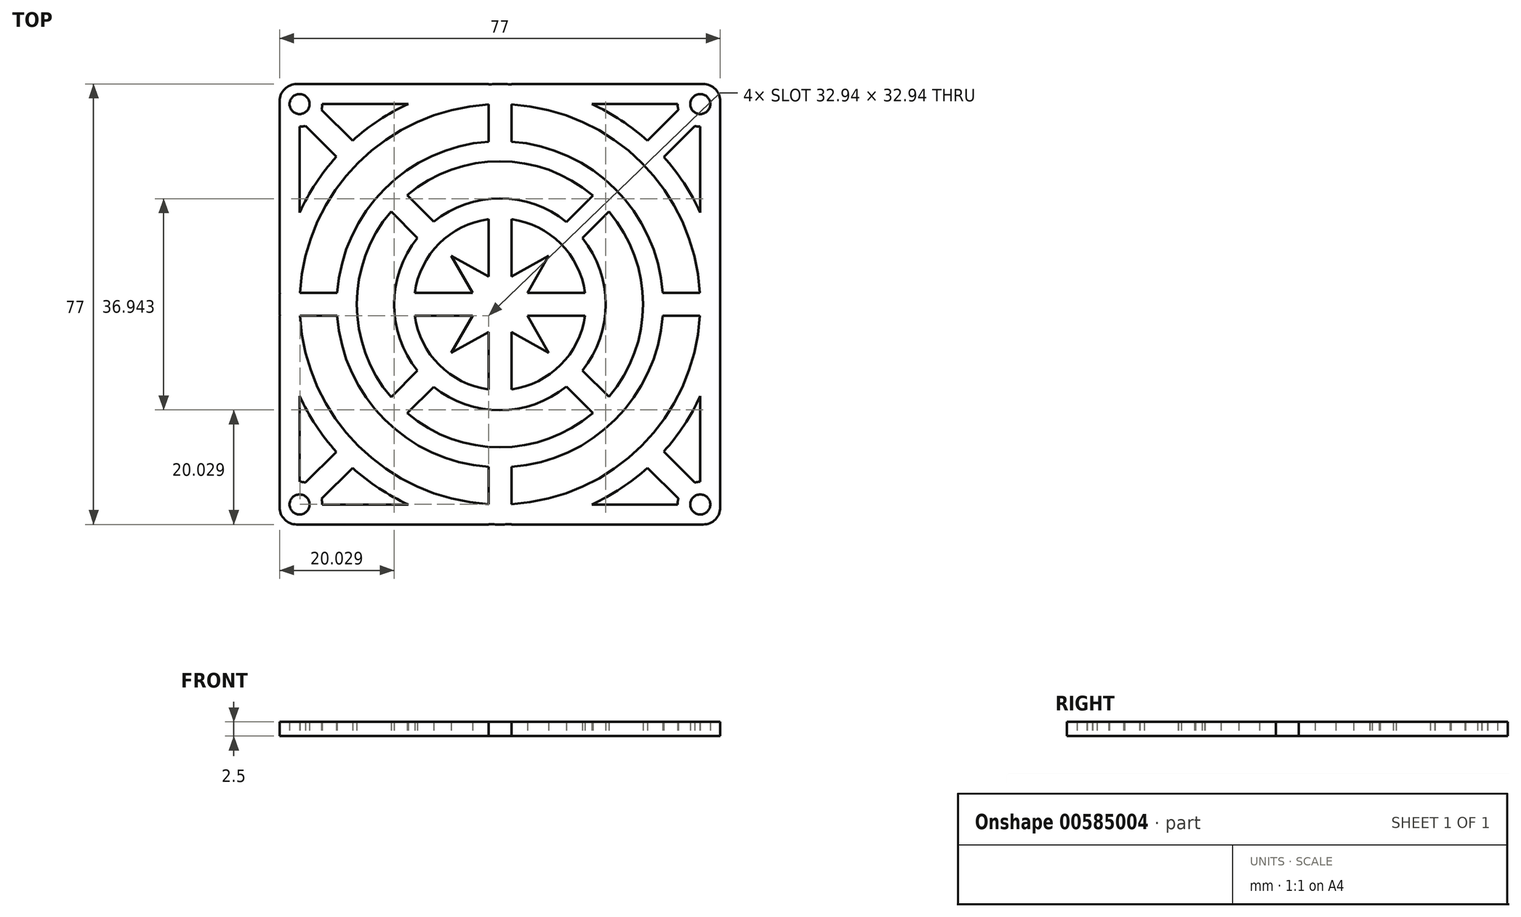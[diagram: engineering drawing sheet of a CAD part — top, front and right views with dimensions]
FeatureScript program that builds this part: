
annotation { "Feature Type Name" : "Feature", "Feature Type Description" : "" }
export const myFeature = defineFeature(function(context is Context, id is Id, definition is map)
    precondition{}
    {
        {
            var Q0;
            Q0=qCreatedBy(makeId("Top.planeOp"),FACE);
            var sketch = newSketch(context, id + "F0", { "sketchPlane" : qUnion([Q0])});
            skLineSegment(sketch, "E0.bottom", {"start": v(-31.05, -35) * mm, "end": v(-16.04, -35) * mm});
            skLineSegment(sketch, "E0.top", {"start": v(-31.05, 35) * mm, "end": v(-16.04, 35) * mm});
            skPoint(sketch, "E0.middle", {"position": v(0, 0) * mm});
            skPoint(sketch, "E1.MirrorCS.end.orphan", {"position": v(34.64, -4.98) * mm});
            skPoint(sketch, "E1.MirrorCS.start.orphan", {"position": v(-34.64, -4.98) * mm});
            skPoint(sketch, "E2.orphan", {"position": v(-34.64, 8.3) * mm});
            skPoint(sketch, "E3.orphan", {"position": v(-34.64, -8.3) * mm});
            skPoint(sketch, "E4.orphan", {"position": v(-34.64, -11.63) * mm});
            skPoint(sketch, "E5.orphan", {"position": v(34.64, -11.63) * mm});
            skPoint(sketch, "E6.orphan", {"position": v(34.64, -8.3) * mm});
            skPoint(sketch, "E7.right.end.orphan", {"position": v(34.64, 8.3) * mm});
            skPoint(sketch, "E8.orphan", {"position": v(-34.64, 4.98) * mm});
            skPoint(sketch, "E9.orphan", {"position": v(34.64, 4.98) * mm});
            skCircle(sketch, "E10", {"center": v(-35, 35) * mm, "radius": 1.75 * mm});
            skCircle(sketch, "E11.MirrorC", {"center": v(35, 35) * mm, "radius": 1.75 * mm});
            skCircle(sketch, "E12.MirrorC", {"center": v(35, -35) * mm, "radius": 1.75 * mm});
            skCircle(sketch, "E13.MirrorC", {"center": v(-35, -35) * mm, "radius": 1.75 * mm});
            skLineSegment(sketch, "E14.bottom", {"start": v(-35.5, -38.5) * mm, "end": v(35.5, -38.5) * mm});
            skLineSegment(sketch, "E14.top", {"start": v(-35.5, 38.5) * mm, "end": v(35.5, 38.5) * mm});
            skLineSegment(sketch, "E14.left", {"start": v(-38.5, -35.5) * mm, "end": v(-38.5, 35.5) * mm});
            skLineSegment(sketch, "E14.right", {"start": v(38.5, -35.5) * mm, "end": v(38.5, 35.5) * mm});
            skPoint(sketch, "E15.visualSharp", {"position": v(38.5, 38.5) * mm});
            skArc(sketch, "E15.filletArc", {"start": v(38.5, 35.5) * mm, "mid": v(37.62, 37.62) * mm, "end": v(35.5, 38.5) * mm});
            skPoint(sketch, "E16.visualSharp", {"position": v(38.5, -38.5) * mm});
            skArc(sketch, "E16.filletArc", {"start": v(35.5, -38.5) * mm, "mid": v(37.62, -37.62) * mm, "end": v(38.5, -35.5) * mm});
            skPoint(sketch, "E17.visualSharp", {"position": v(-38.5, -38.5) * mm});
            skArc(sketch, "E17.filletArc", {"start": v(-38.5, -35.5) * mm, "mid": v(-37.62, -37.62) * mm, "end": v(-35.5, -38.5) * mm});
            skPoint(sketch, "E18.visualSharp", {"position": v(-38.5, 38.5) * mm});
            skArc(sketch, "E18.filletArc", {"start": v(-35.5, 38.5) * mm, "mid": v(-37.62, 37.62) * mm, "end": v(-38.5, 35.5) * mm});
            skArc(sketch, "E19", {"start": v(-28.58, 25.8) * mm, "mid": v(-32.16, 21.16) * mm, "end": v(-35, 16.04) * mm});
            skArc(sketch, "E20", {"start": v(-2, 34.94) * mm, "mid": v(-24.75, 24.75) * mm, "end": v(-34.94, 2) * mm});
            skArc(sketch, "E21", {"start": v(-2, 28.43) * mm, "mid": v(-20.15, 20.15) * mm, "end": v(-28.43, 2) * mm});
            skArc(sketch, "E22", {"start": v(-19.02, 16.23) * mm, "mid": v(-25, 0) * mm, "end": v(-19.02, -16.23) * mm});
            skArc(sketch, "E23", {"start": v(-14.4, 11.6) * mm, "mid": v(-18.5, 0) * mm, "end": v(-14.4, -11.6) * mm});
            skArc(sketch, "E24", {"start": v(-2, 14.87) * mm, "mid": v(-10.6, 10.6) * mm, "end": v(-14.87, 2) * mm});
            skLineSegment(sketch, "E25.bottom", {"start": v(-2, -38.5) * mm, "end": v(2, -38.5) * mm});
            skLineSegment(sketch, "E25.top", {"start": v(-2, 38.5) * mm, "end": v(2, 38.5) * mm});
            skLineSegment(sketch, "E25.left", {"start": v(-2, -38.5) * mm, "end": v(-2, -38.45) * mm});
            skLineSegment(sketch, "E25.right", {"start": v(2, -38.5) * mm, "end": v(2, -38.45) * mm});
            skLineSegment(sketch, "E26.bottom", {"start": v(-38.5, -2) * mm, "end": v(-38.45, -2) * mm});
            skLineSegment(sketch, "E26.top", {"start": v(-38.5, 2) * mm, "end": v(-38.45, 2) * mm});
            skLineSegment(sketch, "E26.left", {"start": v(-38.5, -2) * mm, "end": v(-38.5, 2) * mm});
            skLineSegment(sketch, "E26.right", {"start": v(38.5, -2) * mm, "end": v(38.5, 2) * mm});
            skArc(sketch, "E27", {"start": v(-35, 31.05) * mm, "mid": v(-34.48, 31.08) * mm, "end": v(-33.97, 31.18) * mm});
            skArc(sketch, "E28.MirrorCS", {"start": v(35, 31.05) * mm, "mid": v(34.51, 31.08) * mm, "end": v(34.03, 31.17) * mm});
            skArc(sketch, "E29.MirrorCS", {"start": v(35, -31.05) * mm, "mid": v(34.51, -31.08) * mm, "end": v(34.03, -31.17) * mm});
            skArc(sketch, "E30.MirrorCS", {"start": v(-35, -31.05) * mm, "mid": v(-34.48, -31.08) * mm, "end": v(-33.97, -31.18) * mm});
            skLineSegment(sketch, "E31.trimOffspring", {"start": v(35, -31.05) * mm, "end": v(35, -16.04) * mm});
            skArc(sketch, "E32.trimOffspring", {"start": v(31.18, -33.97) * mm, "mid": v(31.08, -34.48) * mm, "end": v(31.05, -35) * mm});
            skLineSegment(sketch, "E33.trimOffspring", {"start": v(-35, -31.05) * mm, "end": v(-35, -16.04) * mm});
            skLineSegment(sketch, "E34.trimOffspring", {"start": v(16.04, 35) * mm, "end": v(31.05, 35) * mm});
            skLineSegment(sketch, "E35.trimOffspring", {"start": v(-25.75, 28.62) * mm, "end": v(-31.17, 34.03) * mm});
            skLineSegment(sketch, "E36.trimOffspring", {"start": v(-28.58, 25.8) * mm, "end": v(-33.97, 31.18) * mm});
            skLineSegment(sketch, "E37.trimOffspring", {"start": v(-11.57, 14.43) * mm, "end": v(-16.19, 19.05) * mm});
            skLineSegment(sketch, "E38.trimOffspring", {"start": v(-14.4, 11.6) * mm, "end": v(-19.02, 16.23) * mm});
            skLineSegment(sketch, "E39.trimOffspring", {"start": v(-2, 28.43) * mm, "end": v(-2, 35) * mm});
            skLineSegment(sketch, "E40.trimOffspring", {"start": v(2, 28.43) * mm, "end": v(2, 35) * mm});
            skLineSegment(sketch, "E41.trimOffspring", {"start": v(-2, 38.45) * mm, "end": v(-2, 38.5) * mm});
            skLineSegment(sketch, "E42.trimOffspring", {"start": v(2, 38.45) * mm, "end": v(2, 38.5) * mm});
            skLineSegment(sketch, "E43.trimOffspring", {"start": v(25.8, 28.58) * mm, "end": v(31.18, 33.97) * mm});
            skLineSegment(sketch, "E44.trimOffspring", {"start": v(28.62, 25.75) * mm, "end": v(34.03, 31.17) * mm});
            skArc(sketch, "E45.trimOffspring", {"start": v(25.8, 28.58) * mm, "mid": v(21.16, 32.16) * mm, "end": v(16.04, 35) * mm});
            skArc(sketch, "E46.trimOffspring", {"start": v(16.23, 19.02) * mm, "mid": v(0.02, 25) * mm, "end": v(-16.19, 19.05) * mm});
            skArc(sketch, "E47.trimOffspring", {"start": v(11.6, 14.4) * mm, "mid": v(0.02, 18.5) * mm, "end": v(-11.57, 14.43) * mm});
            skLineSegment(sketch, "E48.trimOffspring", {"start": v(11.6, 14.4) * mm, "end": v(16.23, 19.02) * mm});
            skLineSegment(sketch, "E49.trimOffspring", {"start": v(14.43, 11.57) * mm, "end": v(19.05, 16.19) * mm});
            skLineSegment(sketch, "E50.trimOffspring", {"start": v(35, 16.04) * mm, "end": v(35, 31.05) * mm});
            skLineSegment(sketch, "E51.trimOffspring", {"start": v(38.45, 2) * mm, "end": v(38.5, 2) * mm});
            skLineSegment(sketch, "E52.trimOffspring", {"start": v(38.45, -2) * mm, "end": v(38.5, -2) * mm});
            skArc(sketch, "E53.trimOffspring", {"start": v(34.94, 2) * mm, "mid": v(24.75, 24.75) * mm, "end": v(2, 34.94) * mm});
            skLineSegment(sketch, "E54.trimOffspring", {"start": v(28.43, 2) * mm, "end": v(35, 2) * mm});
            skLineSegment(sketch, "E55.trimOffspring", {"start": v(28.43, -2) * mm, "end": v(35, -2) * mm});
            skArc(sketch, "E56.trimOffspring", {"start": v(28.43, 2) * mm, "mid": v(20.15, 20.15) * mm, "end": v(2, 28.43) * mm});
            skArc(sketch, "E57.trimOffspring", {"start": v(14.87, 2) * mm, "mid": v(10.6, 10.6) * mm, "end": v(2, 14.87) * mm});
            skLineSegment(sketch, "E58.trimOffspring", {"start": v(28.62, -25.75) * mm, "end": v(34.03, -31.17) * mm});
            skLineSegment(sketch, "E59.trimOffspring", {"start": v(25.8, -28.58) * mm, "end": v(31.18, -33.97) * mm});
            skArc(sketch, "E60.trimOffspring", {"start": v(28.62, -25.75) * mm, "mid": v(32.18, -21.14) * mm, "end": v(35, -16.04) * mm});
            skArc(sketch, "E61.trimOffspring", {"start": v(19.05, -16.19) * mm, "mid": v(25, 0) * mm, "end": v(19.05, 16.19) * mm});
            skLineSegment(sketch, "E62.trimOffspring", {"start": v(14.43, -11.57) * mm, "end": v(19.05, -16.19) * mm});
            skLineSegment(sketch, "E63.trimOffspring", {"start": v(11.6, -14.4) * mm, "end": v(16.23, -19.02) * mm});
            skArc(sketch, "E64.trimOffspring", {"start": v(14.43, -11.57) * mm, "mid": v(18.5, 0) * mm, "end": v(14.43, 11.57) * mm});
            skLineSegment(sketch, "E65.trimOffspring", {"start": v(16.04, -35) * mm, "end": v(31.05, -35) * mm});
            skLineSegment(sketch, "E66.trimOffspring", {"start": v(-2, -35) * mm, "end": v(-2, -28.43) * mm});
            skLineSegment(sketch, "E67.trimOffspring", {"start": v(2, -35) * mm, "end": v(2, -28.43) * mm});
            skArc(sketch, "E68.trimOffspring", {"start": v(2, -34.94) * mm, "mid": v(24.75, -24.75) * mm, "end": v(34.94, -2) * mm});
            skArc(sketch, "E69.trimOffspring", {"start": v(2, -28.43) * mm, "mid": v(20.15, -20.15) * mm, "end": v(28.43, -2) * mm});
            skLineSegment(sketch, "E70.trimOffspring", {"start": v(-2, -14.87) * mm, "end": v(-2, -4.86) * mm});
            skLineSegment(sketch, "E71.trimOffspring", {"start": v(2, -14.87) * mm, "end": v(2, -4.8) * mm});
            skArc(sketch, "E72.trimOffspring", {"start": v(2, -14.87) * mm, "mid": v(10.6, -10.6) * mm, "end": v(14.87, -2) * mm});
            skArc(sketch, "E73.trimOffspring", {"start": v(-31.17, -34.03) * mm, "mid": v(-31.08, -34.51) * mm, "end": v(-31.05, -35) * mm});
            skArc(sketch, "E74.trimOffspring", {"start": v(31.18, 33.97) * mm, "mid": v(31.08, 34.48) * mm, "end": v(31.05, 35) * mm});
            skArc(sketch, "E75.trimOffspring", {"start": v(-31.17, 34.03) * mm, "mid": v(-31.08, 34.51) * mm, "end": v(-31.05, 35) * mm});
            skArc(sketch, "E76.trimOffspring", {"start": v(-25.75, -28.62) * mm, "mid": v(-21.14, -32.18) * mm, "end": v(-16.04, -35) * mm});
            skLineSegment(sketch, "E77.trimOffspring", {"start": v(-28.58, -25.8) * mm, "end": v(-33.97, -31.18) * mm});
            skLineSegment(sketch, "E78.trimOffspring", {"start": v(-25.75, -28.62) * mm, "end": v(-31.17, -34.03) * mm});
            skArc(sketch, "E79.trimOffspring", {"start": v(-16.19, -19.05) * mm, "mid": v(0.02, -25) * mm, "end": v(16.23, -19.02) * mm});
            skLineSegment(sketch, "E80.trimOffspring", {"start": v(-14.4, -11.6) * mm, "end": v(-19.02, -16.23) * mm});
            skArc(sketch, "E81.trimOffspring", {"start": v(-11.57, -14.43) * mm, "mid": v(0.02, -18.5) * mm, "end": v(11.6, -14.4) * mm});
            skLineSegment(sketch, "E82.trimOffspring", {"start": v(-11.57, -14.43) * mm, "end": v(-16.19, -19.05) * mm});
            skLineSegment(sketch, "E83.trimOffspring", {"start": v(-35, -2) * mm, "end": v(-35, 0) * mm});
            skLineSegment(sketch, "E84.trimOffspring", {"start": v(-35, 16.04) * mm, "end": v(-35, 31.05) * mm});
            skArc(sketch, "E85.trimOffspring", {"start": v(-34.94, -2) * mm, "mid": v(-24.75, -24.75) * mm, "end": v(-2, -34.94) * mm});
            skLineSegment(sketch, "E86.trimOffspring", {"start": v(-34.94, 2) * mm, "end": v(-28.43, 2) * mm});
            skLineSegment(sketch, "E87.trimOffspring", {"start": v(-35, -2) * mm, "end": v(-28.43, -2) * mm});
            skLineSegment(sketch, "E88.trimOffspring", {"start": v(-14.87, 2) * mm, "end": v(-4.8, 2) * mm});
            skLineSegment(sketch, "E89.trimOffspring", {"start": v(-14.87, -2) * mm, "end": v(-4.8, -2) * mm});
            skArc(sketch, "E90.trimOffspring", {"start": v(-28.43, -2) * mm, "mid": v(-20.15, -20.15) * mm, "end": v(-2, -28.43) * mm});
            skArc(sketch, "E91.trimOffspring", {"start": v(-14.87, -2) * mm, "mid": v(-10.6, -10.6) * mm, "end": v(-2, -14.87) * mm});
            skArc(sketch, "E92.trimOffspring", {"start": v(-38.45, 2) * mm, "mid": v(-38.5, 0) * mm, "end": v(-38.45, -2) * mm});
            skArc(sketch, "E93.trimOffspring", {"start": v(-35, -16.04) * mm, "mid": v(-32.16, -21.16) * mm, "end": v(-28.58, -25.8) * mm});
            skArc(sketch, "E94.trimOffspring", {"start": v(35, 16.04) * mm, "mid": v(32.18, 21.14) * mm, "end": v(28.62, 25.75) * mm});
            skArc(sketch, "E95.trimOffspring", {"start": v(2, 38.45) * mm, "mid": v(0, 38.5) * mm, "end": v(-2, 38.45) * mm});
            skArc(sketch, "E96.trimOffspring", {"start": v(-16.04, 35) * mm, "mid": v(-21.14, 32.18) * mm, "end": v(-25.75, 28.62) * mm});
            skArc(sketch, "E97.trimOffspring", {"start": v(38.45, -2) * mm, "mid": v(38.5, 0) * mm, "end": v(38.45, 2) * mm});
            skArc(sketch, "E98.trimOffspring", {"start": v(16.04, -35) * mm, "mid": v(21.16, -32.16) * mm, "end": v(25.8, -28.58) * mm});
            skArc(sketch, "E99.trimOffspring", {"start": v(-2, -38.45) * mm, "mid": v(0, -38.5) * mm, "end": v(2, -38.45) * mm});
            skLineSegment(sketch, "E100", {"start": v(-4.8, 2) * mm, "end": v(-8.5, 8.5) * mm});
            skLineSegment(sketch, "E101", {"start": v(-2, 4.86) * mm, "end": v(-8.5, 8.5) * mm});
            skLineSegment(sketch, "E102.MirrorCS", {"start": v(2, 4.86) * mm, "end": v(8.5, 8.5) * mm});
            skLineSegment(sketch, "E103.MirrorCS", {"start": v(4.8, 2) * mm, "end": v(8.5, 8.5) * mm});
            skLineSegment(sketch, "E104.MirrorCS", {"start": v(4.8, -2) * mm, "end": v(8.5, -8.5) * mm});
            skLineSegment(sketch, "E105.MirrorCS", {"start": v(2, -4.86) * mm, "end": v(8.5, -8.5) * mm});
            skLineSegment(sketch, "E106.MirrorCS", {"start": v(-2, -4.86) * mm, "end": v(-8.5, -8.5) * mm});
            skLineSegment(sketch, "E107.MirrorCS", {"start": v(-4.8, -2) * mm, "end": v(-8.5, -8.5) * mm});
            skLineSegment(sketch, "E108.trimOffspring", {"start": v(4.8, 2) * mm, "end": v(14.87, 2) * mm});
            skLineSegment(sketch, "E109.trimOffspring", {"start": v(2, 4.8) * mm, "end": v(2, 14.87) * mm});
            skLineSegment(sketch, "E110.trimOffspring", {"start": v(4.8, -2) * mm, "end": v(14.87, -2) * mm});
            skPoint(sketch, "E111.orphan", {"position": v(-4.8, -2) * mm});
            skLineSegment(sketch, "E112.trimOffspring", {"start": v(-2, 4.86) * mm, "end": v(-2, 14.87) * mm});
            skPoint(sketch, "E113.trimOffspring.end.orphan", {"position": v(2, -4.8) * mm});
            skPoint(sketch, "E114.trimOffspring.end.orphan", {"position": v(4.86, 2) * mm});
            skPoint(sketch, "E115.trimOffspring.end.orphan", {"position": v(4.86, -2) * mm});
            skSolve(sketch);
        }
        {
            var Q0;
            Q0=makeQuery(id+"F0.imprint","IMPRINT",FACE,{"disambiguationData":[TD([[makeQuery(id+"F0.imprint","IMPRINT",EDGE,{"derivedFrom":sQuery(id+"F0.wireOp",EDGE,"E0.bottom")}),-1.0]])]});
            extrude(context, id + "F1", {"entities" : qUnion([Q0]), "depth" : 2.5 * mm, "offsetDistance" : 25 * mm});
        }
    });
